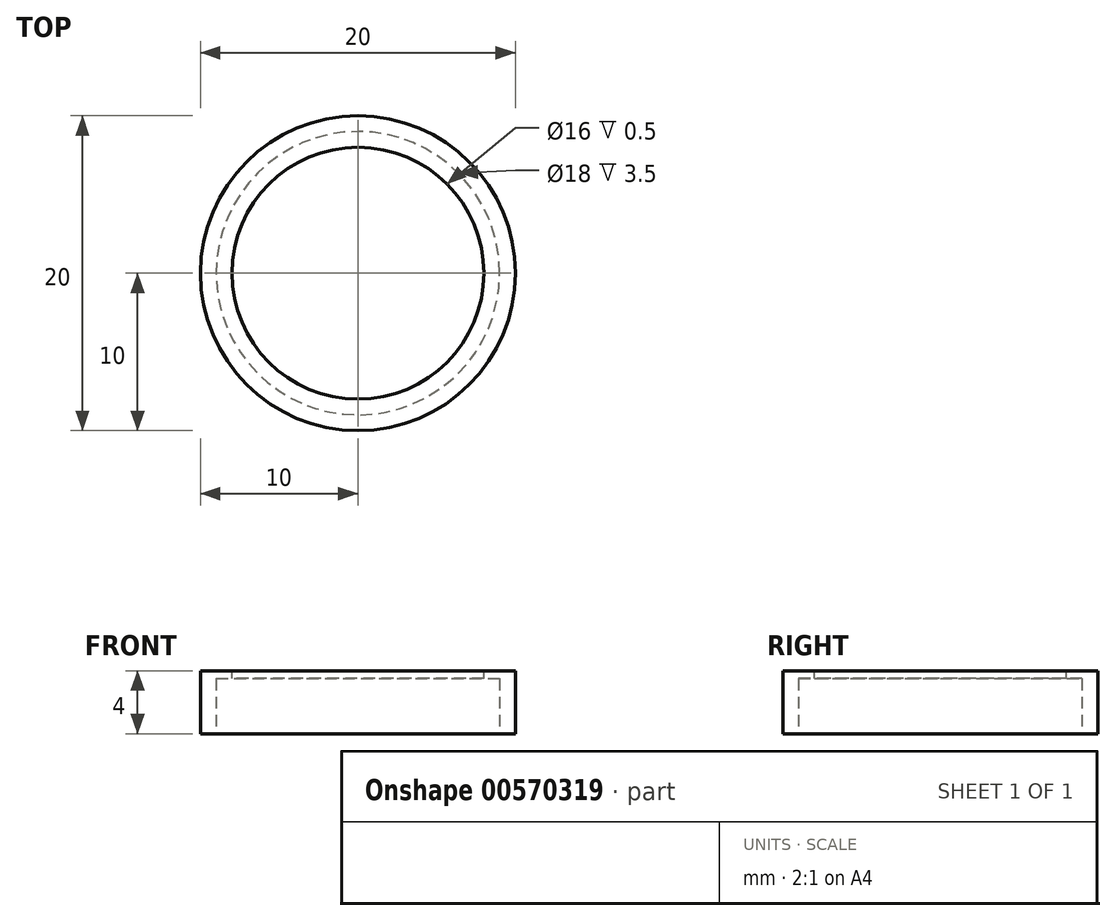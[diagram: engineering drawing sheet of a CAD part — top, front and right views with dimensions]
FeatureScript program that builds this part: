
annotation { "Feature Type Name" : "Feature", "Feature Type Description" : "" }
export const myFeature = defineFeature(function(context is Context, id is Id, definition is map)
    precondition{}
    {
        {
            var Q0;
            Q0=qCreatedBy(makeId("Top.planeOp"),FACE);
            var sketch = newSketch(context, id + "F0", { "sketchPlane" : qUnion([Q0])});
            skCircle(sketch, "E0", {"center": v(0, 0) * mm, "radius": 10 * mm});
            skSolve(sketch);
        }
        {
            var Q0;
            Q0 = qSketchRegion(id + "F0", true);
            var Q1;
            Q1=makeQuery(id+"F0.imprint","IMPRINT",FACE,{"disambiguationData":[TD([[makeQuery(id+"F0.imprint","IMPRINT",EDGE,{"derivedFrom":sQuery(id+"F0.wireOp",EDGE,"E0")}),1.0]])]});
            extrude(context, id + "F1", {"entities" : qUnion([Q0, Q1]), "depth" : 4 * mm, "offsetDistance" : 25 * mm});
        }
        {
            var Q0;
            Q0=makeQuery(id+"F1.opExtrude","CAP_FACE",FACE,{"disambiguationData":[OSD([sQuery(id+"F0.wireOp",EDGE,"E0")])],"isStart":false});
            var sketch = newSketch(context, id + "F2", { "sketchPlane" : qUnion([Q0])});
            skCircle(sketch, "E1", {"center": v(0, 0) * mm, "radius": 8 * mm});
            skSolve(sketch);
        }
        {
            var Q0;
            Q0 = qSketchRegion(id + "F2", true);
            extrude(context, id + "F3", {"entities" : qUnion([Q0]), "operationType" : NewBodyOperationType.REMOVE, "oppositeDirection" : true, "depth" : 25 * mm, "offsetDistance" : 25 * mm});
        }
        {
            var Q0;
            Q0=makeQuery(id+"F1.opExtrude","CAP_FACE",FACE,{"disambiguationData":[OSD([sQuery(id+"F0.wireOp",EDGE,"E0")])],"isStart":true});
            var sketch = newSketch(context, id + "F4", { "sketchPlane" : qUnion([Q0])});
            skCircle(sketch, "E2", {"center": v(0, 0) * mm, "radius": 9 * mm});
            skSolve(sketch);
        }
        {
            var Q0;
            Q0=makeQuery(id+"F4.imprint","IMPRINT",FACE,{"disambiguationData":[TD([[makeQuery(id+"F4.imprint","IMPRINT",EDGE,{"derivedFrom":sQuery(id+"F4.wireOp",EDGE,"E2")}),1.0]])]});
            extrude(context, id + "F5", {"entities" : qUnion([Q0]), "operationType" : NewBodyOperationType.REMOVE, "oppositeDirection" : true, "depth" : 3.5 * mm, "offsetDistance" : 25 * mm});
        }
    });
